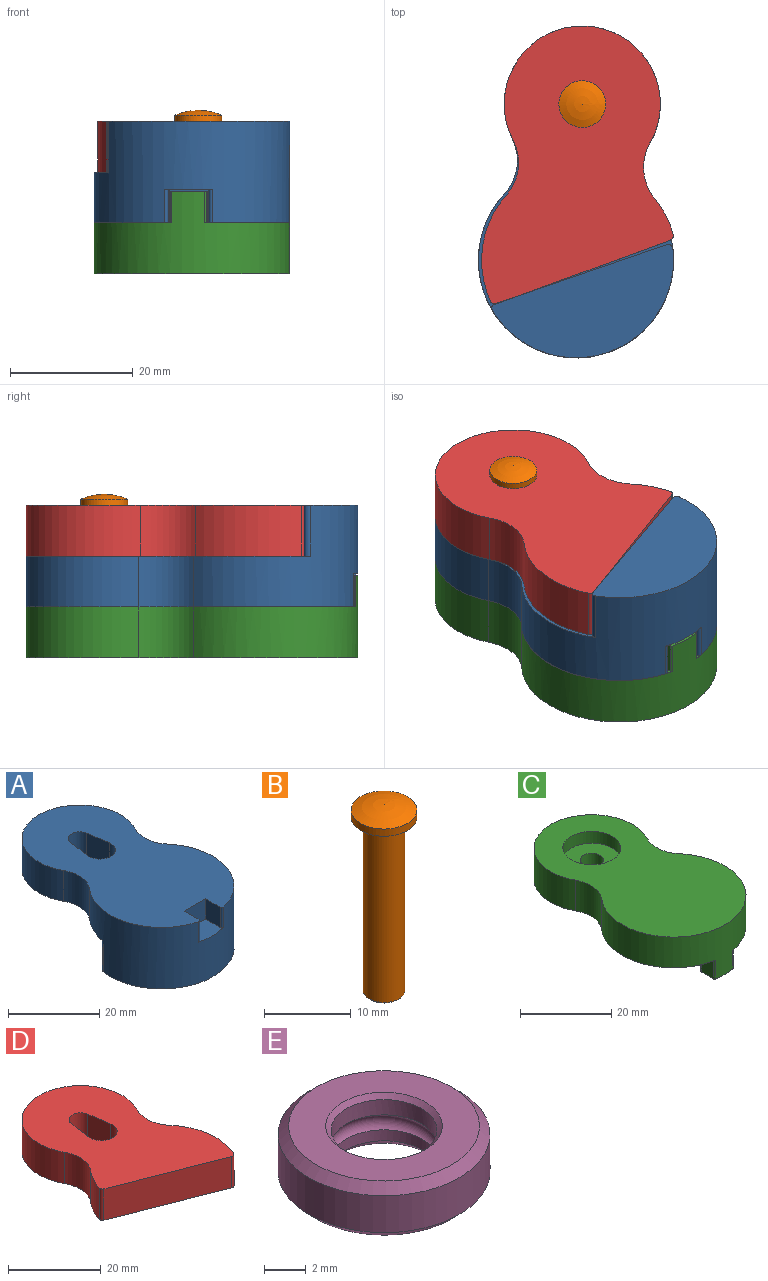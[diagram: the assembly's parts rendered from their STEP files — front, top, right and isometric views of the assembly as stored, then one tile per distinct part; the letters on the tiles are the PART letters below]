
ASSEMBLY  parts=5 mates=7
PART A: 20 faces, bbox 31.8x54x16.5 mm
  f0: plane 53.5x31.75mm, normal (0,0,1), area 1189.5mm2, adj f2,f3,f4,f5,f6,f7,f8,f9
  f1: plane 46.85x31.55mm, normal (0,0,-1), area 907mm2, adj f2,f3,f4,f5,f6,f7,f8,f9
  f2: cylinder r=7.95mm len=8.98mm, axis (0,0,-1), area 79.3mm2, adj f0,f1,f3,f5
  f3: cylinder r=15.88mm len=31.75mm, axis (0,0,-1), area 909.7mm2, adj f0,f1,f2,f4,f11,f15,f16,f17
  f4: cylinder r=7.95mm len=8.98mm, axis (0,0,-1), area 79.3mm2, adj f0,f1,f3,f5
  f5: cylinder r=12.7mm len=25.4mm, axis (0,0,-1), area 434.5mm2, adj f0,f1,f2,f4
  f6: cylinder r=2.54mm len=8.26mm, axis (0,0,-1), area 59.9mm2, adj f0,f1,f7,f9
  f7: plane 8.26x6.1mm, normal (0.99,-0.14,0), area 50.8mm2, adj f0,f1,f6,f8
  f8: cylinder r=3.43mm len=8.26mm, axis (0,0,-1), area 97mm2, adj f0,f1,f7,f9
  f9: plane 8.26x6.1mm, normal (-0.99,-0.14,0), area 50.8mm2, adj f0,f1,f6,f8
  f10: plane 27.53x10.73mm, normal (0.36,0.93,0), area 243.9mm2, adj f1,f11,f16,f17
  f11: plane 29.25x19.03mm, normal (0,0,-1), area 318.8mm2, adj f3,f10,f16,f17
  f12: plane 5.46x4.6mm, normal (1,0,0), area 25.1mm2, adj f0,f14,f15,f18
  f13: plane 5.46x4.6mm, normal (-1,0,0), area 25.1mm2, adj f0,f14,f15,f19
  f14: plane 6.6x5.46mm, normal (0,-1,0), area 36.1mm2, adj f0,f12,f13,f15
  f15: plane 7.87x5.59mm, normal (0,0,1), area 36.3mm2, adj f3,f12,f13,f14,f18,f19
  f16: cylinder r=0.76mm len=8.26mm, axis (0,0,-1), area 11.2mm2, adj f1,f3,f10,f11
  f17: cylinder r=0.76mm len=8.26mm, axis (0,0,-1), area 11.2mm2, adj f1,f3,f10,f11
  f18: cylinder r=0.51mm len=5.46mm, axis (0,0,-1), area 5.1mm2, adj f0,f3,f12,f15
  f19: cylinder r=0.51mm len=5.46mm, axis (0,0,-1), area 5.1mm2, adj f0,f3,f13,f15
PART B: 6 faces, bbox 7.6x7.6x26.6 mm
  f0: plane 4.32x4.32mm, normal (0,0,-1), area 14.6mm2, adj f5
  f1: cylinder r=2.41mm len=24.51mm, axis (0,0,1), area 371.6mm2, adj f2,f5
  f2: plane 7.62x7.62mm, normal (0,0,-1), area 27.3mm2, adj f1,f3
  f3: cylinder r=3.81mm len=7.62mm, axis (0,0,1), area 24.3mm2, adj f2,f4
  f4: sphere r=9.53mm, area 47.6mm2, adj f3
  f5: cone r=2.41mm half-angle=45deg, axis (0,0,1), area 5.2mm2, adj f0,f1
PART C: 19 faces, bbox 31.8x54x13.3 mm
  f0: cylinder r=2.54mm len=5.08mm, axis (0,0,-1), area 81.1mm2, adj f1,f18
  f1: plane 53.74x31.75mm, normal (0,0,-1), area 736.8mm2, adj f0,f2,f3,f4,f5,f7,f8,f9
  f2: cylinder r=7.95mm len=8.98mm, axis (0,0,-1), area 79.3mm2, adj f1,f3,f5,f6
  f3: cylinder r=15.88mm len=31.75mm, axis (0,0,-1), area 624.8mm2, adj f1,f2,f4,f6,f12,f15,f16
  f4: cylinder r=7.95mm len=8.98mm, axis (0,0,-1), area 79.3mm2, adj f1,f3,f5,f6
  f5: cylinder r=12.7mm len=25.4mm, axis (0,0,-1), area 434.5mm2, adj f1,f2,f4,f6
  f6: plane 53.98x31.75mm, normal (0,0,1), area 1165.2mm2, adj f2,f3,f4,f5,f17
  f7: plane 5.08x3.71mm, normal (-1,0,0), area 18.8mm2, adj f1,f11,f12,f15
  f8: plane 5.08x3.71mm, normal (1,0,0), area 18.8mm2, adj f1,f9,f12,f16
  f9: cylinder r=0.76mm len=5.08mm, axis (0,0,1), area 6.1mm2, adj f1,f8,f10,f12
  f10: plane 5.08x4.32mm, normal (0,1,0), area 21.9mm2, adj f1,f9,f11,f12
  f11: cylinder r=0.76mm len=5.08mm, axis (0,0,1), area 6.1mm2, adj f1,f7,f10,f12
  f12: plane 5.84x4.95mm, normal (0,0,-1), area 28.1mm2, adj f3,f7,f8,f9,f10,f11,f15,f16
  f13: cylinder r=12.7mm len=25.4mm, axis (0,0,-1), area 506.7mm2, adj f1,f14
  f14: plane 25.4x25.4mm, normal (0,0,-1), area 506.7mm2, adj f13
  f15: cylinder r=0.25mm len=5.08mm, axis (0,0,-1), area 1.8mm2, adj f1,f3,f7,f12
  f16: cylinder r=0.25mm len=5.08mm, axis (0,0,-1), area 1.8mm2, adj f1,f3,f8,f12
  f17: cylinder r=6.35mm len=12.7mm, axis (0,0,1), area 126.7mm2, adj f6,f18
  f18: plane 12.7x12.7mm, normal (0,0,1), area 106.4mm2, adj f0,f17
PART D: 15 faces, bbox 31.1x45.5x8.3 mm
  f0: cylinder r=7.95mm len=8.98mm, axis (0,0,-1), area 79.3mm2, adj f1,f5,f6,f7
  f1: cylinder r=15.88mm len=8.26mm, axis (0,0,-1), area 55.1mm2, adj f0,f6,f7,f13
  f2: plane 28.06x10.93mm, normal (-0.36,-0.93,0), area 248.6mm2, adj f6,f7,f13,f14
  f3: cylinder r=15.88mm len=17.31mm, axis (0,0,-1), area 152.5mm2, adj f4,f6,f7,f14
  f4: cylinder r=7.95mm len=8.98mm, axis (0,0,-1), area 79.3mm2, adj f3,f5,f6,f7
  f5: cylinder r=12.7mm len=25.4mm, axis (0,0,-1), area 434.5mm2, adj f0,f4,f6,f7
  f6: plane 45.52x31.13mm, normal (0,0,1), area 894.5mm2, adj f0,f1,f2,f3,f4,f5,f8,f9
  f7: plane 45.52x31.13mm, normal (0,0,-1), area 940.3mm2, adj f0,f1,f2,f3,f4,f5,f8,f13
  f8: cylinder r=2.54mm len=8.26mm, axis (0,0,1), area 70.9mm2, adj f6,f7,f9,f11,f12
  f9: plane 6.99x6.1mm, normal (0.99,-0.14,0), area 43mm2, adj f6,f8,f10,f12
  f10: cylinder r=3.43mm len=6.99mm, axis (0,0,1), area 82.1mm2, adj f6,f9,f11,f12
  f11: plane 6.99x6.1mm, normal (-0.99,-0.14,0), area 43mm2, adj f6,f8,f10,f12
  f12: plane 10.02x6.86mm, normal (0,0,1), area 45.9mm2, adj f8,f9,f10,f11
  f13: cylinder r=0.76mm len=8.26mm, axis (0,0,-1), area 9.3mm2, adj f1,f2,f6,f7
  f14: cylinder r=0.76mm len=8.26mm, axis (0,0,-1), area 9.3mm2, adj f2,f3,f6,f7
PART E: 10 faces, bbox 10.2x10.2x3.2 mm
  f0: cylinder r=2.54mm len=5.08mm, axis (0,0,-1), area 10.2mm2, adj f5,f9
  f1: cylinder r=2.54mm len=5.08mm, axis (0,0,-1), area 14.3mm2, adj f8,f9
  f2: cylinder r=5.08mm len=10.16mm, axis (0,0,-1), area 68.9mm2, adj f6,f7
  f3: plane 9.14x9.14mm, normal (0,0,1), area 41.1mm2, adj f7,f8
  f4: plane 9.14x9.14mm, normal (0,0,-1), area 36.5mm2, adj f5,f6
  f5: cone r=3.05mm half-angle=45deg, axis (0,0,-1), area 12.6mm2, adj f0,f4
  f6: cone r=5.08mm half-angle=45deg, axis (0,0,1), area 21.8mm2, adj f2,f4
  f7: cone r=4.57mm half-angle=45deg, axis (0,0,-1), area 21.8mm2, adj f2,f3
  f8: cone r=2.54mm half-angle=45deg, axis (0,0,1), area 6mm2, adj f1,f3
  f9: torus R=2.29mm, axis (0,0,-1), area 18.1mm2, adj f0,f1
PLACE A rot(axis=(0.02,1,0),180deg) t=(30.12,24.96,48.5)mm
PLACE B rot(axis=(0,0,-1),1.1deg) t=(-122.22,28.78,31.99)mm
PLACE C rot(axis=(0.02,1,0),180deg) t=(68.19,23.43,40.25)mm fixed
PLACE D rot(axis=(-0.01,-1,0),180deg) t=(-7.95,26.49,56.76)mm
PLACE E rot(axis=(0,0,-1),2.3deg) t=(-134.85,31.59,31.99)mm
MATE planar A.f0 <-> C.f5  axis (0,0,-1) through (-8.57,11.05,40.25)mm
MATE planar E.f2 <-> C.f17  axis (0,0,1) through (-7.95,26.49,35.17)mm
MATE planar D.f6 <-> A.f1  axis (0,0,-1) through (3.81,11.17,48.5)mm
MATE cylindrical B.f1 <-> D.f8  axis (0,0,1) through (-7.95,26.49,44.5)mm
MATE cylindrical C.f0 <-> D.f8  axis (0,0,1) through (-7.95,26.49,37.71)mm
MATE planar B.f1 <-> D.f7  axis (0,0,-1) through (-7.95,26.49,56.76)mm
MATE cylindrical E.f0 <-> B.f1  axis (0,0,-1) through (-7.95,26.49,34.47)mm
